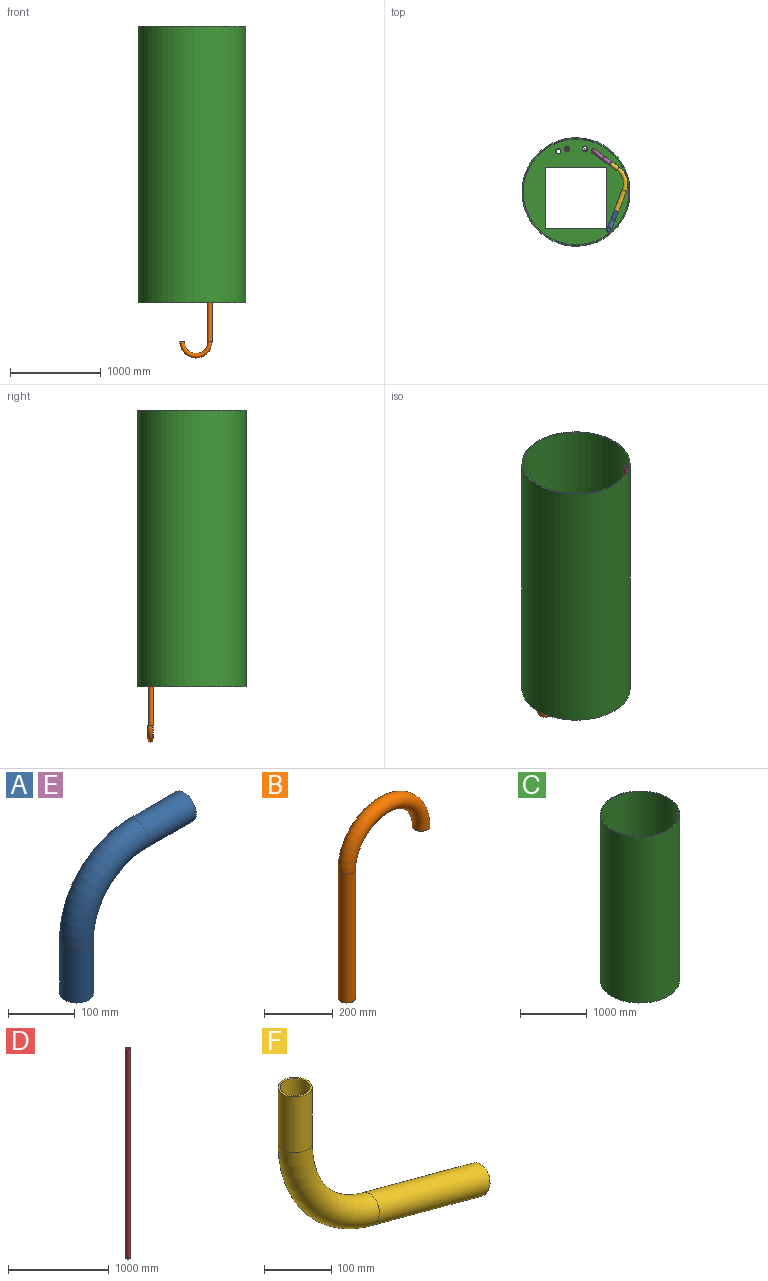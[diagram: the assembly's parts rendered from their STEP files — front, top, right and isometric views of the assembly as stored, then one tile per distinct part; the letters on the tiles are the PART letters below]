
ASSEMBLY  parts=6 mates=11
PART A: 8 faces, bbox 266.6x50.8x266.6 mm
  f0: cylinder r=22.23mm len=101.6mm, axis (0,0,1), area 14187.8mm2, adj f1,f3
  f1: torus R=127mm, axis (0,1,0), area 27857.7mm2, adj f0,f2
  f2: cylinder r=22.23mm len=101.6mm, axis (1,0,0), area 14187.8mm2, adj f1,f4
  f3: plane 50.8x50.8mm, normal (0,0,-1), area 475mm2, adj f0,f5
  f4: plane 50.8x50.8mm, normal (1,0,0), area 475mm2, adj f2,f7
  f5: cylinder r=25.4mm len=101.6mm, axis (0,0,1), area 16214.6mm2, adj f3,f6
  f6: torus R=127mm, axis (0,1,0), area 31837.4mm2, adj f5,f7
  f7: cylinder r=25.4mm len=101.6mm, axis (1,0,0), area 16214.6mm2, adj f4,f6
PART B: 6 faces, bbox 384.9x50.8x649.6 mm
  f0: cylinder r=22.23mm len=457.2mm, axis (0,0,1), area 63845.1mm2, adj f1,f2
  f1: torus R=152.4mm, axis (0,1,0), area 66858.5mm2, adj f0,f3
  f2: plane 50.8x50.8mm, normal (0,0,-1), area 475mm2, adj f0,f4
  f3: plane 50.8x50.8mm, normal (0,0,-1), area 475mm2, adj f1,f5
  f4: cylinder r=25.4mm len=457.2mm, axis (0,0,1), area 72965.9mm2, adj f2,f5
  f5: torus R=152.4mm, axis (0,1,0), area 76409.7mm2, adj f3,f4
PART C: 21 faces, bbox 1190.7x1190.7x3048 mm
  f0: plane 673.1x12.7mm, normal (-1,0,0), area 8548.4mm2, adj f1,f6,f8,f9
  f1: plane 673.1x12.7mm, normal (0,1,0), area 8548.4mm2, adj f0,f2,f8,f9
  f2: plane 673.1x12.7mm, normal (1,0,0), area 8548.4mm2, adj f1,f6,f8,f9
  f3: cylinder r=25.4mm len=50.8mm, axis (0,0,-1), area 8107.3mm2, adj f9,f16
  f4: cylinder r=25.4mm len=50.8mm, axis (0,0,-1), area 8107.3mm2, adj f9,f18
  f5: cylinder r=25.4mm len=50.8mm, axis (0,0,-1), area 8107.3mm2, adj f9,f20
  f6: plane 673.1x12.7mm, normal (0,-1,0), area 8548.4mm2, adj f0,f2,f8,f9
  f7: cylinder r=25.4mm len=50.8mm, axis (0,0,-1), area 8107.3mm2, adj f9,f14
  f8: plane 1165.27x1165.27mm, normal (0,0,1), area 603137.2mm2, adj f0,f1,f2,f6,f10,f13,f15,f17
  f9: plane 1190.67x1190.67mm, normal (0,0,-1), area 652289.8mm2, adj f0,f1,f2,f3,f4,f5,f6,f7
  f10: cylinder r=582.64mm len=3035.3mm, axis (0,0,-1), area 11111666mm2, adj f8,f12
  f11: cylinder r=595.34mm len=3048mm, axis (0,0,-1), area 11401377.9mm2, adj f9,f12
  f12: plane 1190.67x1190.67mm, normal (0,0,1), area 46999mm2, adj f10,f11
  f13: cylinder r=28.57mm len=57.15mm, axis (0,0,-1), area 6840.6mm2, adj f8,f14
  f14: plane 57.15x57.15mm, normal (0,0,1), area 538.4mm2, adj f7,f13
  f15: cylinder r=28.57mm len=57.15mm, axis (0,0,-1), area 6840.6mm2, adj f8,f16
  f16: plane 57.15x57.15mm, normal (0,0,1), area 538.4mm2, adj f3,f15
  f17: cylinder r=28.57mm len=57.15mm, axis (0,0,-1), area 6840.6mm2, adj f8,f18
  f18: plane 57.15x57.15mm, normal (0,0,1), area 538.4mm2, adj f4,f17
  f19: cylinder r=28.57mm len=57.15mm, axis (0,0,-1), area 6840.6mm2, adj f8,f20
  f20: plane 57.15x57.15mm, normal (0,0,1), area 538.4mm2, adj f5,f19
PART D: 4 faces, bbox 50.8x50.8x2540 mm
  f0: plane 50.8x50.8mm, normal (0,0,1), area 475mm2, adj f2,f3
  f1: plane 50.8x50.8mm, normal (0,0,-1), area 475mm2, adj f2,f3
  f2: cylinder r=25.4mm len=2540mm, axis (0,0,-1), area 405366mm2, adj f0,f1
  f3: cylinder r=22.23mm len=2540mm, axis (0,0,-1), area 354695.2mm2, adj f0,f1
PART E: same geometry as A
PART F: 8 faces, bbox 434.5x50.8x384.9 mm
  f0: cylinder r=22.23mm len=101.6mm, axis (0,0,-1), area 14187.8mm2, adj f1,f3
  f1: torus R=203.2mm, axis (0,-1,0), area 37143.6mm2, adj f0,f2
  f2: cylinder r=22.23mm len=244.58mm, axis (0.97,0,-0.26), area 33696mm2, adj f1,f4
  f3: plane 50.8x50.8mm, normal (0,0,1), area 475mm2, adj f0,f5
  f4: plane 50.8x49.07mm, normal (0.97,0,-0.26), area 475mm2, adj f2,f7
  f5: cylinder r=25.4mm len=101.6mm, axis (0,0,-1), area 16214.6mm2, adj f3,f6
  f6: torus R=203.2mm, axis (0,-1,0), area 42449.8mm2, adj f5,f7
  f7: cylinder r=25.4mm len=246.23mm, axis (0.97,0,-0.26), area 38509.8mm2, adj f4,f6
PLACE A rot(axis=(0.49,-0.72,0.49),108.6deg) t=(466.1,-219.98,268.36)mm
PLACE B rot(axis=(-0.02,-1,0),180deg) t=(217.72,437.56,39.76)mm
PLACE C t=(22.19,-76.45,14.36)mm fixed
PLACE D rot(axis=(-0.11,0.99,0),180deg) t=(383.35,-433.07,3036.96)mm
PLACE E rot(axis=(0,0,-1),36.2deg) t=(217.72,437.56,39.76)mm
PLACE F rot(axis=(0.34,-0.67,-0.67),142.7deg) t=(402.14,302.48,268.36)mm
MATE planar E.f7 <-> F.f5  axis (0.81,-0.59,0) through (402.14,302.48,268.36)mm
MATE parallel D.f2 <-> C.f10  axis (0,0,-1) through (383.35,-433.07,496.96)mm
MATE cylindrical A.f5 <-> F.f2  axis (0.36,0.93,0) through (466.1,-219.98,268.36)mm
MATE planar F.f2 <-> A.f5  axis (-0.36,-0.93,0) through (466.1,-219.98,268.36)mm
MATE planar E.f5 <-> B.f4  axis (0,0,-1) through (217.72,437.56,39.76)mm
MATE planar B.f4 <-> C.f5  axis (0,0,1) through (217.72,437.56,39.76)mm
MATE cylindrical E.f5 <-> B.f4  axis (0,0,1) through (217.72,437.56,39.76)mm
MATE cylindrical B.f4 <-> C.f5  axis (0,0,1) through (217.72,437.56,39.76)mm
MATE planar D.f2 <-> A.f7  axis (0,0,-1) through (383.35,-433.07,496.96)mm
MATE cylindrical F.f5 <-> E.f7  axis (0.81,-0.59,0) through (402.14,302.48,268.36)mm
MATE cylindrical D.f3 <-> A.f7  axis (0,0,-1) through (383.35,-433.07,496.96)mm
